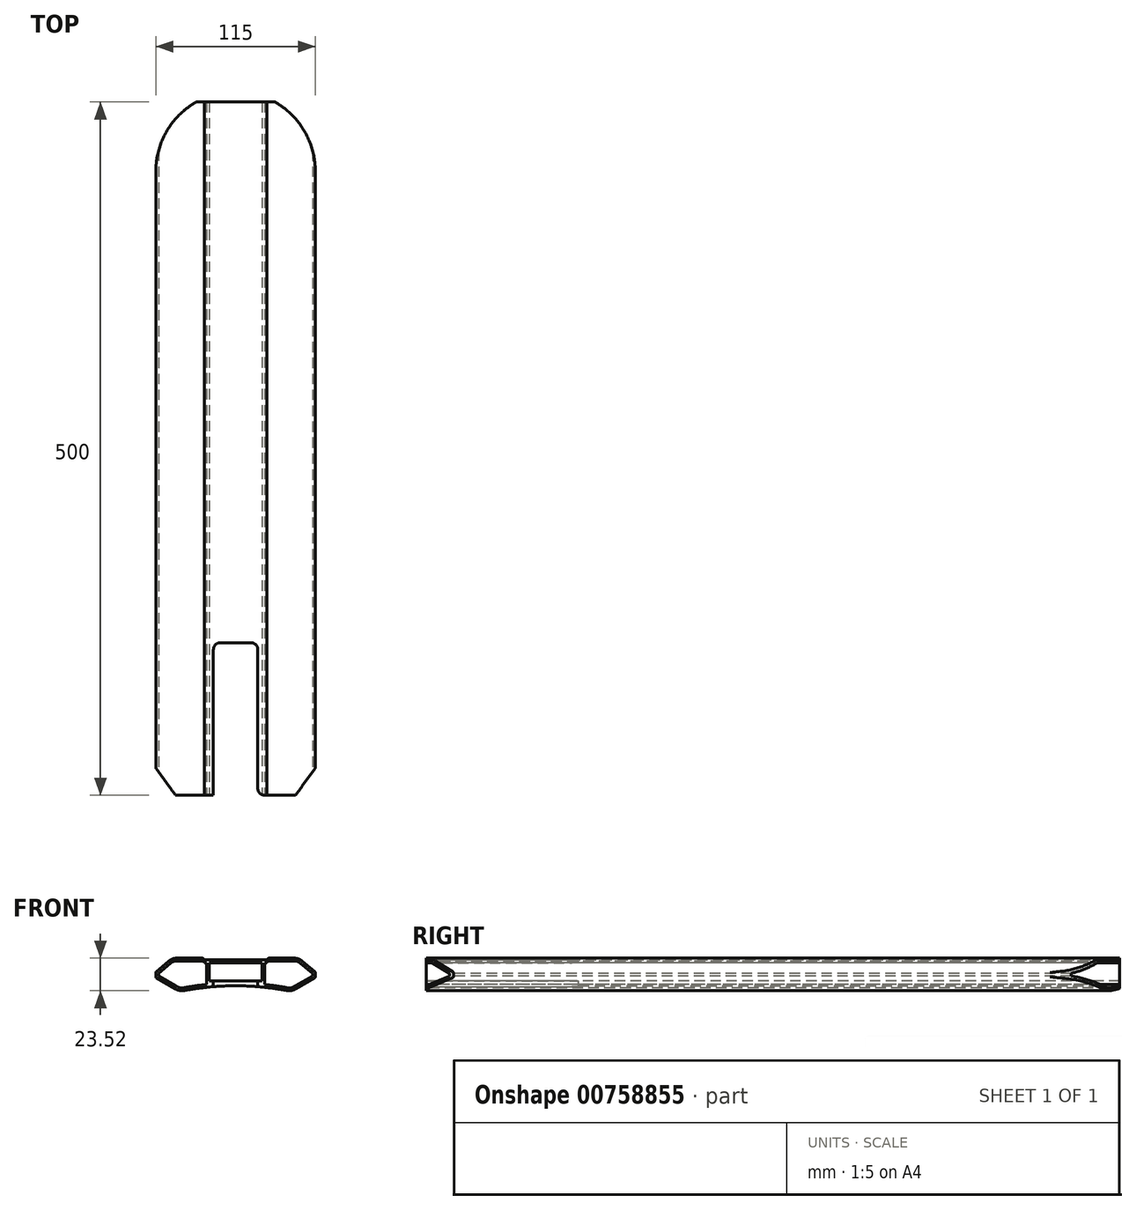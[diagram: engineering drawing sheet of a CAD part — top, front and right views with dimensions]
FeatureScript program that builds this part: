
annotation { "Feature Type Name" : "Feature", "Feature Type Description" : "" }
export const myFeature = defineFeature(function(context is Context, id is Id, definition is map)
    precondition{}
    {
        {
            var Q0;
            Q0=qCreatedBy(makeId("Front.planeOp"),FACE);
            var sketch = newSketch(context, id + "F0", { "sketchPlane" : qUnion([Q0])});
            skLineSegment(sketch, "E0", {"start": v(-45.58, 10) * mm, "end": v(-22.5, 10) * mm});
            skLineSegment(sketch, "E1", {"start": v(-45.58, 10) * mm, "end": v(-57.5, 0) * mm});
            skLineSegment(sketch, "E2", {"start": v(-40.18, -14) * mm, "end": v(-57.5, -4) * mm});
            skLineSegment(sketch, "E3", {"start": v(-22.5, 10) * mm, "end": v(-22.5, 8.7) * mm});
            skLineSegment(sketch, "E4", {"start": v(-22.5, 8.7) * mm, "end": v(22.5, 8.7) * mm});
            skLineSegment(sketch, "E5", {"start": v(22.5, 8.7) * mm, "end": v(22.5, 10) * mm});
            skLineSegment(sketch, "E6", {"start": v(22.5, 10) * mm, "end": v(45.58, 10) * mm});
            skLineSegment(sketch, "E7", {"start": v(45.58, 10) * mm, "end": v(57.5, 0) * mm});
            skLineSegment(sketch, "E8", {"start": v(57.5, 0) * mm, "end": v(57.5, -4) * mm});
            skLineSegment(sketch, "E9", {"start": v(57.5, -4) * mm, "end": v(40.18, -14) * mm});
            skArc(sketch, "E10", {"start": v(40.18, -14) * mm, "mid": v(0, -9.92) * mm, "end": v(-40.18, -14) * mm});
            skLineSegment(sketch, "E11", {"start": v(-57.5, 0) * mm, "end": v(-57.5, -4) * mm});
            skSolve(sketch);
        }
        {
            var Q0;
            Q0=qCreatedBy(makeId("Front.planeOp"),FACE);
            var sketch = newSketch(context, id + "F1", { "sketchPlane" : qUnion([Q0])});
            skLineSegment(sketch, "E12", {"start": v(0, 0) * mm, "end": v(0, 28.18) * mm, "construction": true});
            skSolve(sketch);
        }
        {
            var Q0;
            Q0=makeQuery(id+"F0.imprint","IMPRINT",FACE,{"disambiguationData":[TD([[makeQuery(id+"F0.imprint","IMPRINT",EDGE,{"derivedFrom":sQuery(id+"F0.wireOp",EDGE,"E0")}),-1.0]])]});
            extrude(context, id + "F2", {"entities" : qUnion([Q0]), "endBound" : BoundingType.SYMMETRIC, "depth" : 500 * mm, "offsetDistance" : 25 * mm});
        }
        {
            var Q0;
            Q0=qCreatedBy(makeId("Front.planeOp"),FACE);
            var sketch = newSketch(context, id + "F3", { "sketchPlane" : qUnion([Q0])});
            skLineSegment(sketch, "E13.bottom", {"start": v(-19, 6.7) * mm, "end": v(19, 6.7) * mm});
            skLineSegment(sketch, "E13.top", {"start": v(-19, -6.3) * mm, "end": v(19, -6.3) * mm});
            skLineSegment(sketch, "E13.left", {"start": v(-19, 6.7) * mm, "end": v(-19, -6.3) * mm});
            skLineSegment(sketch, "E13.right", {"start": v(19, 6.7) * mm, "end": v(19, -6.3) * mm});
            skSolve(sketch);
        }
        {
            var Q0;
            Q0 = qSketchRegion(id + "F3", true);
            extrude(context, id + "F4", {"entities" : qUnion([Q0]), "operationType" : NewBodyOperationType.REMOVE, "endBound" : BoundingType.SYMMETRIC, "oppositeDirection" : true, "depth" : 500 * mm, "offsetDistance" : 25 * mm});
        }
        {
            var Q0;
            Q0=makeQuery(id+"F2.opExtrude","SWEPT_EDGE",EDGE,{"disambiguationData":[OSD([sQuery(id+"F0.wireOp",EDGE,"E6"),sQuery(id+"F0.wireOp",EDGE,"E7")])]});
            var Q1;
            Q1=makeQuery(id+"F2.opExtrude","SWEPT_EDGE",EDGE,{"disambiguationData":[OSD([sQuery(id+"F0.wireOp",EDGE,"E9"),sQuery(id+"F0.wireOp",EDGE,"E10")])]});
            var Q2;
            Q2=makeQuery(id+"F2.opExtrude","SWEPT_EDGE",EDGE,{"disambiguationData":[OSD([sQuery(id+"F0.wireOp",EDGE,"E0"),sQuery(id+"F0.wireOp",EDGE,"E1")])]});
            var Q3;
            Q3=makeQuery(id+"F2.opExtrude","SWEPT_EDGE",EDGE,{"disambiguationData":[OSD([sQuery(id+"F0.wireOp",EDGE,"E2"),sQuery(id+"F0.wireOp",EDGE,"E10")])]});
            fillet(context, id + "F5", {"entities" : qUnion([Q0, Q1, Q2, Q3]), "radius" : 9 * mm, "tangentPropagation" : true, "allowEdgeOverflow" : false});
        }
        {
            var Q0;
            Q0=makeQuery(id+"F2.opExtrude","SWEPT_EDGE",EDGE,{"disambiguationData":[OSD([sQuery(id+"F0.wireOp",EDGE,"E7"),sQuery(id+"F0.wireOp",EDGE,"E8")])]});
            var Q1;
            Q1=makeQuery(id+"F2.opExtrude","SWEPT_EDGE",EDGE,{"disambiguationData":[OSD([sQuery(id+"F0.wireOp",EDGE,"E8"),sQuery(id+"F0.wireOp",EDGE,"E9")])]});
            var Q2;
            Q2=makeQuery(id+"F2.opExtrude","SWEPT_EDGE",EDGE,{"disambiguationData":[OSD([sQuery(id+"F0.wireOp",EDGE,"E1"),sQuery(id+"F0.wireOp",EDGE,"E11")])]});
            var Q3;
            Q3=makeQuery(id+"F2.opExtrude","SWEPT_EDGE",EDGE,{"disambiguationData":[OSD([sQuery(id+"F0.wireOp",EDGE,"E2"),sQuery(id+"F0.wireOp",EDGE,"E11")])]});
            fillet(context, id + "F6", {"entities" : qUnion([Q0, Q1, Q2, Q3]), "radius" : 1 * mm, "tangentPropagation" : true, "allowEdgeOverflow" : false});
        }
        {
            var Q0;
            Q0=makeQuery(id+"F2.opExtrude","SWEPT_EDGE",EDGE,{"disambiguationData":[OSD([sQuery(id+"F0.wireOp",EDGE,"E5"),sQuery(id+"F0.wireOp",EDGE,"E6")])]});
            var Q1;
            Q1=makeQuery(id+"F2.opExtrude","SWEPT_EDGE",EDGE,{"disambiguationData":[OSD([sQuery(id+"F0.wireOp",EDGE,"E0"),sQuery(id+"F0.wireOp",EDGE,"E3")])]});
            fillet(context, id + "F7", {"entities" : qUnion([Q0, Q1]), "radius" : 2 * mm, "tangentPropagation" : true, "allowEdgeOverflow" : false});
        }
        {
            var Q0;
            Q0=makeQuery(id+"F2.opExtrude","CAP_FACE",FACE,{"disambiguationData":[OSD([sQuery(id+"F0.wireOp",EDGE,"E0"),sQuery(id+"F0.wireOp",EDGE,"E1"),sQuery(id+"F0.wireOp",EDGE,"E2"),sQuery(id+"F0.wireOp",EDGE,"E3"),sQuery(id+"F0.wireOp",EDGE,"E4"),sQuery(id+"F0.wireOp",EDGE,"E5"),sQuery(id+"F0.wireOp",EDGE,"E6"),sQuery(id+"F0.wireOp",EDGE,"E7"),sQuery(id+"F0.wireOp",EDGE,"E8"),sQuery(id+"F0.wireOp",EDGE,"E9"),sQuery(id+"F0.wireOp",EDGE,"E10"),sQuery(id+"F0.wireOp",EDGE,"E11")])],"isStart":false});
            var sketch = newSketch(context, id + "F8", { "sketchPlane" : qUnion([Q0])});
            skLineSegment(sketch, "E14.0.0", {"start": v(42.3, 10) * mm, "end": v(24.37, 10) * mm});
            skArc(sketch, "E14.0.1", {"start": v(24.37, 10) * mm, "mid": v(23.23, 9.64) * mm, "end": v(22.5, 8.7) * mm});
            skLineSegment(sketch, "E14.0.3", {"start": v(21, 6.7) * mm, "end": v(21, -9.02) * mm});
            skLineSegment(sketch, "E14.0.5", {"start": v(-21, -9.02) * mm, "end": v(-21, 6.7) * mm});
            skArc(sketch, "E14.0.7", {"start": v(-22.5, 8.7) * mm, "mid": v(-23.23, 9.64) * mm, "end": v(-24.37, 10) * mm});
            skLineSegment(sketch, "E14.0.8", {"start": v(-24.37, 10) * mm, "end": v(-42.3, 10) * mm});
            skArc(sketch, "E14.0.9", {"start": v(-42.3, 10) * mm, "mid": v(-45.38, 9.46) * mm, "end": v(-48.1, 7.9) * mm});
            skLineSegment(sketch, "E14.0.10", {"start": v(-48.1, 7.9) * mm, "end": v(-57.14, 0.3) * mm});
            skArc(sketch, "E14.0.11", {"start": v(-57.14, 0.3) * mm, "mid": v(-57.4, -0.04) * mm, "end": v(-57.5, -0.47) * mm});
            skLineSegment(sketch, "E14.0.12", {"start": v(-57.5, -0.47) * mm, "end": v(-57.5, -3.42) * mm});
            skArc(sketch, "E14.0.13", {"start": v(-57.5, -3.42) * mm, "mid": v(-57.37, -3.92) * mm, "end": v(-57, -4.29) * mm});
            skLineSegment(sketch, "E14.0.14", {"start": v(-57, -4.29) * mm, "end": v(-43.1, -12.31) * mm});
            skArc(sketch, "E14.0.15", {"start": v(-43.1, -12.31) * mm, "mid": v(-40.12, -13.4) * mm, "end": v(-36.94, -13.36) * mm});
            skArc(sketch, "E14.0.16", {"start": v(-36.94, -13.36) * mm, "mid": v(0, -9.92) * mm, "end": v(36.94, -13.36) * mm});
            skArc(sketch, "E14.0.17", {"start": v(36.94, -13.36) * mm, "mid": v(40.12, -13.4) * mm, "end": v(43.1, -12.31) * mm});
            skLineSegment(sketch, "E14.0.18", {"start": v(43.1, -12.31) * mm, "end": v(57, -4.29) * mm});
            skArc(sketch, "E14.0.19", {"start": v(57, -4.29) * mm, "mid": v(57.37, -3.92) * mm, "end": v(57.5, -3.42) * mm});
            skLineSegment(sketch, "E14.0.20", {"start": v(57.5, -3.42) * mm, "end": v(57.5, -0.47) * mm});
            skArc(sketch, "E14.0.21", {"start": v(57.5, -0.47) * mm, "mid": v(57.4, -0.04) * mm, "end": v(57.14, 0.3) * mm});
            skLineSegment(sketch, "E14.0.22", {"start": v(57.14, 0.3) * mm, "end": v(48.1, 7.9) * mm});
            skArc(sketch, "E14.0.23", {"start": v(48.1, 7.9) * mm, "mid": v(45.38, 9.46) * mm, "end": v(42.3, 10) * mm});
            skArc(sketch, "E15.0", {"start": v(-37.3, -11.4) * mm, "mid": v(-29.18, -10.04) * mm, "end": v(-21, -9.02) * mm});
            skArc(sketch, "E15.1", {"start": v(-42.1, -10.58) * mm, "mid": v(-39.78, -11.42) * mm, "end": v(-37.3, -11.4) * mm});
            skLineSegment(sketch, "E15.2", {"start": v(-55.5, -2.85) * mm, "end": v(-42.1, -10.58) * mm});
            skLineSegment(sketch, "E15.3", {"start": v(-24.37, 8) * mm, "end": v(-42.3, 8) * mm});
            skArc(sketch, "E15.4", {"start": v(-42.3, 8) * mm, "mid": v(-44.7, 7.58) * mm, "end": v(-46.8, 6.36) * mm});
            skLineSegment(sketch, "E15.5", {"start": v(-46.8, 6.36) * mm, "end": v(-55.5, -0.93) * mm});
            skLineSegment(sketch, "E15.6", {"start": v(-55.5, -0.93) * mm, "end": v(-55.5, -2.85) * mm});
            skLineSegment(sketch, "E16.0", {"start": v(-22.5, 6.7) * mm, "end": v(21, 6.7) * mm});
            skArc(sketch, "E17", {"start": v(-24.37, 8) * mm, "mid": v(-23.23, 7.64) * mm, "end": v(-22.5, 6.7) * mm});
            skArc(sketch, "E18.MirrorCS", {"start": v(37.3, -11.4) * mm, "mid": v(29.18, -10.04) * mm, "end": v(21, -9.02) * mm});
            skArc(sketch, "E19.MirrorCS", {"start": v(42.1, -10.58) * mm, "mid": v(39.78, -11.42) * mm, "end": v(37.3, -11.4) * mm});
            skLineSegment(sketch, "E20.MirrorCS", {"start": v(55.5, -2.85) * mm, "end": v(42.1, -10.58) * mm});
            skLineSegment(sketch, "E21.MirrorCS", {"start": v(55.5, -0.93) * mm, "end": v(55.5, -2.85) * mm});
            skLineSegment(sketch, "E22.MirrorCS", {"start": v(46.8, 6.36) * mm, "end": v(55.5, -0.93) * mm});
            skArc(sketch, "E23.MirrorCS", {"start": v(42.3, 8) * mm, "mid": v(44.7, 7.58) * mm, "end": v(46.8, 6.36) * mm});
            skLineSegment(sketch, "E24.MirrorCS", {"start": v(24.37, 8) * mm, "end": v(42.3, 8) * mm});
            skArc(sketch, "E25.MirrorCS", {"start": v(24.37, 8) * mm, "mid": v(23.23, 7.64) * mm, "end": v(22.5, 6.7) * mm});
            skLineSegment(sketch, "E26.MirrorCS", {"start": v(22.5, 6.7) * mm, "end": v(-21, 6.7) * mm});
            skSolve(sketch);
        }
        {
            var Q0;
            Q0=makeQuery(id+"F8.imprint","IMPRINT",FACE,{"disambiguationData":[TD([[makeQuery(id+"F8.imprint","IMPRINT",EDGE,{"derivedFrom":sQuery(id+"F8.wireOp",EDGE,"E14.0.5")}),1.0]])]});
            var Q1;
            {var subQ0=sQuery(id+"F8.wireOp",EDGE,"E14.0.3");Q1=makeQuery(id+"F8.imprint","IMPRINT",FACE,{"disambiguationData":[TD([[makeQuery(id+"F8.imprint","IMPRINT",EDGE,{"derivedFrom":subQ0}),1.0]])]});}
            extrude(context, id + "F9", {"entities" : qUnion([Q0, Q1]), "operationType" : NewBodyOperationType.REMOVE, "endBound" : BoundingType.THROUGH_ALL, "oppositeDirection" : true, "depth" : 25 * mm, "offsetDistance" : 25 * mm});
        }
        {
            var Q0;
            Q0=qCreatedBy(makeId("Top.planeOp"),FACE);
            var sketch = newSketch(context, id + "F10", { "sketchPlane" : qUnion([Q0])});
            skArc(sketch, "E27", {"start": v(57.5, 200) * mm, "mid": v(0, 257.5) * mm, "end": v(-57.5, 200) * mm});
            skLineSegment(sketch, "E28", {"start": v(57.5, 280) * mm, "end": v(57.5, 200) * mm});
            skLineSegment(sketch, "E29", {"start": v(-57.5, 200) * mm, "end": v(-57.5, 280) * mm});
            skLineSegment(sketch, "E30", {"start": v(57.5, 280) * mm, "end": v(-57.5, 280) * mm});
            skSolve(sketch);
        }
        {
            var Q0;
            Q0=qCreatedBy(makeId("Top.planeOp"),FACE);
            var sketch = newSketch(context, id + "F11", { "sketchPlane" : qUnion([Q0])});
            skLineSegment(sketch, "E31", {"start": v(22.5, -120.52) * mm, "end": v(-22.5, -120.52) * mm});
            skLineSegment(sketch, "E32", {"start": v(68, -346) * mm, "end": v(68, -216) * mm});
            skLineSegment(sketch, "E33", {"start": v(68, -216) * mm, "end": v(43.3, -250) * mm});
            skLineSegment(sketch, "E34", {"start": v(43.3, -250) * mm, "end": v(16, -250) * mm});
            skLineSegment(sketch, "E35", {"start": v(16, -250) * mm, "end": v(16, -140) * mm});
            skLineSegment(sketch, "E36", {"start": v(16, -140) * mm, "end": v(-16, -140) * mm});
            skLineSegment(sketch, "E37", {"start": v(-16, -140) * mm, "end": v(-16, -250) * mm});
            skLineSegment(sketch, "E38", {"start": v(-16, -250) * mm, "end": v(-43.3, -250) * mm});
            skLineSegment(sketch, "E39", {"start": v(-43.3, -250) * mm, "end": v(-68, -216) * mm});
            skLineSegment(sketch, "E40", {"start": v(-68, -216) * mm, "end": v(-68, -346) * mm});
            skLineSegment(sketch, "E41", {"start": v(-68, -346) * mm, "end": v(68, -346) * mm});
            skPoint(sketch, "E42.endSnap0", {"position": v(0, -346) * mm});
            skPoint(sketch, "E42.endSnap1", {"position": v(0, -120.52) * mm});
            skSolve(sketch);
        }
        {
            var Q0;
            Q0 = qSketchRegion(id + "F11", true);
            extrude(context, id + "F12", {"entities" : qUnion([Q0]), "operationType" : NewBodyOperationType.REMOVE, "endBound" : BoundingType.THROUGH_ALL, "oppositeDirection" : true, "depth" : 25 * mm, "offsetDistance" : 25 * mm, "hasSecondDirection" : true, "secondDirectionBound" : SecondDirectionBoundingType.THROUGH_ALL, "secondDirectionOppositeDirection" : false, "secondDirectionDepth" : 25 * mm});
        }
        {
            var Q0;
            {var subQ0=sQuery(id+"F0.wireOp",EDGE,"E10");var subQ1=sQuery(id+"F11.wireOp",EDGE,"E37");Q0=makeQuery(id+"F12.boolean.opBoolean","COPY",EDGE,{"disambiguationData":[TD([makeQuery(id+"F2.opExtrude","SWEPT_FACE",FACE,{"disambiguationData":[OSD([subQ0])]})])],"derivedFrom":makeQuery(id+"F12.opExtrude","SWEPT_EDGE",EDGE,{"disambiguationData":[OSD([subQ1,sQuery(id+"F11.wireOp",EDGE,"E38")])]})});}
            var Q1;
            {var subQ0=sQuery(id+"F11.wireOp",EDGE,"E36");var subQ1=sQuery(id+"F11.wireOp",EDGE,"E37");Q1=makeQuery(id+"F12.boolean.opBoolean","COPY",EDGE,{"disambiguationData":[TD([makeQuery(id+"F2.opExtrude","SWEPT_FACE",FACE,{"disambiguationData":[OSD([sQuery(id+"F0.wireOp",EDGE,"E10")])]})])],"derivedFrom":makeQuery(id+"F12.opExtrude","SWEPT_EDGE",EDGE,{"disambiguationData":[OSD([subQ0,subQ1])]})});}
            var Q2;
            {var subQ0=sQuery(id+"F11.wireOp",EDGE,"E36");var subQ1=sQuery(id+"F11.wireOp",EDGE,"E37");Q2=makeQuery(id+"F12.boolean.opBoolean","COPY",EDGE,{"disambiguationData":[TD([makeQuery(id+"F2.opExtrude","SWEPT_FACE",FACE,{"disambiguationData":[OSD([sQuery(id+"F0.wireOp",EDGE,"E4")])]})])],"derivedFrom":makeQuery(id+"F12.opExtrude","SWEPT_EDGE",EDGE,{"disambiguationData":[OSD([subQ0,subQ1])]})});}
            var Q3;
            {var subQ0=sQuery(id+"F11.wireOp",EDGE,"E36");var subQ1=sQuery(id+"F11.wireOp",EDGE,"E35");Q3=makeQuery(id+"F12.boolean.opBoolean","COPY",EDGE,{"disambiguationData":[TD([makeQuery(id+"F2.opExtrude","SWEPT_FACE",FACE,{"disambiguationData":[OSD([sQuery(id+"F0.wireOp",EDGE,"E10")])]})])],"derivedFrom":makeQuery(id+"F12.opExtrude","SWEPT_EDGE",EDGE,{"disambiguationData":[OSD([subQ1,subQ0])]})});}
            var Q4;
            {var subQ0=sQuery(id+"F11.wireOp",EDGE,"E35");var subQ1=sQuery(id+"F11.wireOp",EDGE,"E36");Q4=makeQuery(id+"F12.boolean.opBoolean","COPY",EDGE,{"disambiguationData":[TD([makeQuery(id+"F2.opExtrude","SWEPT_FACE",FACE,{"disambiguationData":[OSD([sQuery(id+"F0.wireOp",EDGE,"E4")])]})])],"derivedFrom":makeQuery(id+"F12.opExtrude","SWEPT_EDGE",EDGE,{"disambiguationData":[OSD([subQ0,subQ1])]})});}
            var Q5;
            {var subQ0=sQuery(id+"F0.wireOp",EDGE,"E4");var subQ1=sQuery(id+"F11.wireOp",EDGE,"E35");Q5=makeQuery(id+"F12.boolean.opBoolean","COPY",EDGE,{"disambiguationData":[TD([makeQuery(id+"F2.opExtrude","SWEPT_FACE",FACE,{"disambiguationData":[OSD([subQ0])]})])],"derivedFrom":makeQuery(id+"F12.opExtrude","SWEPT_EDGE",EDGE,{"disambiguationData":[OSD([sQuery(id+"F11.wireOp",EDGE,"E34"),subQ1])]})});}
            fillet(context, id + "F13", {"entities" : qUnion([Q0, Q1, Q2, Q3, Q4, Q5]), "radius" : 5 * mm, "tangentPropagation" : true, "allowEdgeOverflow" : false});
        }
        {
            var Q0;
            Q0=makeQuery(id+"F10.imprint","IMPRINT",FACE,{"disambiguationData":[TD([[makeQuery(id+"F10.imprint","IMPRINT",EDGE,{"derivedFrom":sQuery(id+"F10.wireOp",EDGE,"E27")}),-1.0]])]});
            extrude(context, id + "F14", {"entities" : qUnion([Q0]), "operationType" : NewBodyOperationType.REMOVE, "endBound" : BoundingType.THROUGH_ALL, "oppositeDirection" : true, "depth" : 25 * mm, "offsetDistance" : 25 * mm, "hasSecondDirection" : true, "secondDirectionBound" : SecondDirectionBoundingType.THROUGH_ALL, "secondDirectionOppositeDirection" : false, "secondDirectionDepth" : 25 * mm});
        }
    });
